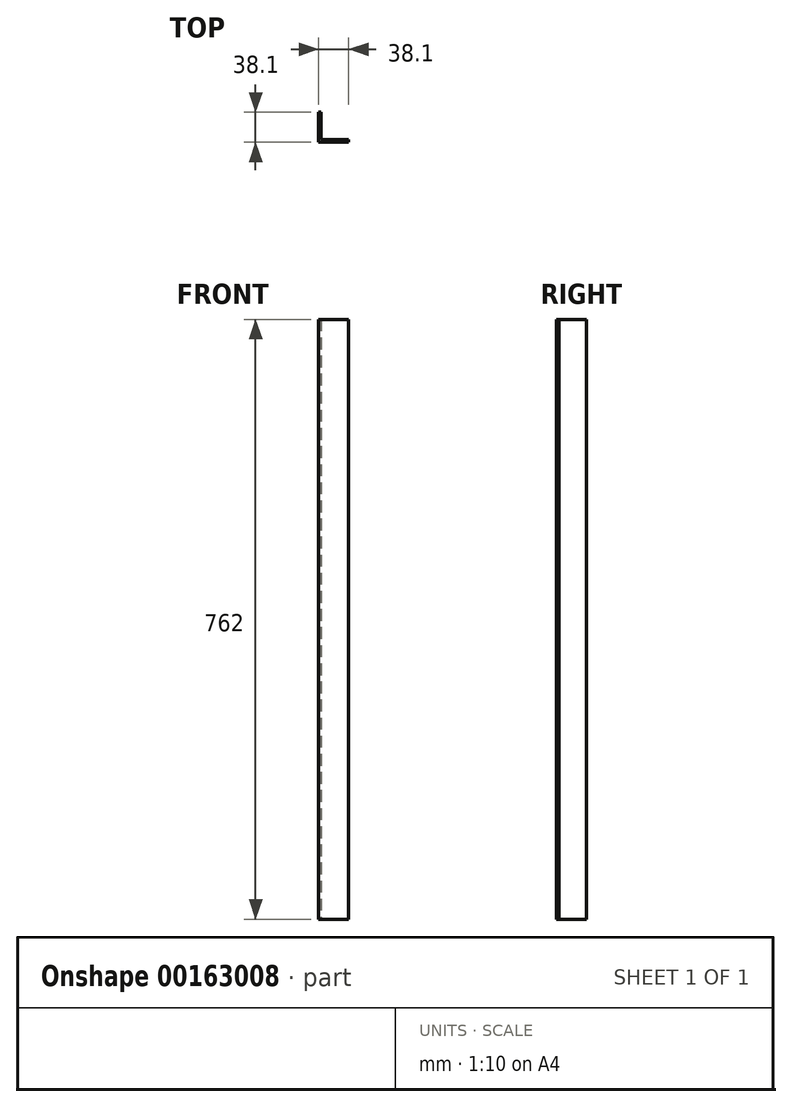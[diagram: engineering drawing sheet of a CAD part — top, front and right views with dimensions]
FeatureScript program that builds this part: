
annotation { "Feature Type Name" : "Feature", "Feature Type Description" : "" }
export const myFeature = defineFeature(function(context is Context, id is Id, definition is map)
    precondition{}
    {
        {
            var Q0;
            Q0=qCreatedBy(makeId("Top.planeOp"),FACE);
            var sketch = newSketch(context, id + "F0", { "sketchPlane" : qUnion([Q0])});
            skLineSegment(sketch, "E0", {"start": v(0, 38.1) * mm, "end": v(0, 0) * mm});
            skLineSegment(sketch, "E1", {"start": v(0, 0) * mm, "end": v(38.1, 0) * mm});
            skLineSegment(sketch, "E2.0", {"start": v(3.18, 3.18) * mm, "end": v(38.1, 3.18) * mm});
            skLineSegment(sketch, "E2.1", {"start": v(3.17, 38.1) * mm, "end": v(3.18, 3.18) * mm});
            skLineSegment(sketch, "E3", {"start": v(0, 38.1) * mm, "end": v(3.17, 38.1) * mm});
            skLineSegment(sketch, "E4", {"start": v(38.1, 3.18) * mm, "end": v(38.1, 0) * mm});
            skSolve(sketch);
        }
        {
            var Q0;
            Q0 = qSketchRegion(id + "F0", true);
            extrude(context, id + "F1", {"entities" : qUnion([Q0]), "depth" : 762 * mm});
        }
    });
